FCSTD DOCUMENT  (FreeCAD 0.20R29603 (Git))
Label: chair_seat_support
License: Creative Commons Attribution
LicenseURL: http://creativecommons.org/licenses/by/4.0/
objects: Sketcher::SketchObject×1, PartDesign::Body×1
note: 2 computed .brp shape members not serialized (recipe doc carries the construction recipe); baked Part::Feature solids carry a one-line shape summary decoded from their .brp

FEATURE [Sketcher::SketchObject] Sketch
  FullyConstrained = false
  MapMode = 5
  Placement = pos=(0,0,0) rot=(1,0,0;1.5708rad)
  Support = -> [XZ_Plane]
  sketch-geometry (5):
    g0: LineSegment StartX=-112.903 StartY=-38.7593 StartZ=0 EndX=-112.903 EndY=38.7593 EndZ=0
    g1: LineSegment StartX=-112.903 StartY=38.7593 StartZ=0 EndX=112.903 EndY=38.7593 EndZ=0
    g2: LineSegment StartX=112.903 StartY=38.7593 StartZ=0 EndX=112.903 EndY=-38.7593 EndZ=0
    g3: LineSegment StartX=112.903 StartY=-38.7593 StartZ=0 EndX=-112.903 EndY=-38.7593 EndZ=0
    g4: GeomPoint X=0 Y=0 Z=0
  constraints (10):
    c: Coincident(g0,g1)
    c: Coincident(g1,g2)
    c: Coincident(g2,g3)
    c: Coincident(g3,g0)
    c: Horizontal(g1)
    c: Horizontal(g3)
    c: Vertical(g0)
    c: Vertical(g2)
    c: Symmetric(g1,g0,g4)
    c: Coincident(g4,g-1)
FEATURE [PartDesign::Body] Body
  Group = -> [Sketch]
  Origin = -> Origin
